# Revit family: FP_Revit_18_CG244DLPX1_N_Cooktop_90001824A
name_source: partatom
category: Specialty Equipment
revit_build: Autodesk Revit 2018 (Build: 20170223_1515(x64)
units: mm (PartAtom-declared; Revit-internal decimal feet)

## family parameters
Always vertical = Yes
Cut with Voids When Loaded = Yes
OmniClass Number = 23.40.40.00
OmniClass Title = Food Service Equipment and Furnishings
Part Type = Normal
Room Calculation Point = No
Round Connector Dimension = Use Diameter
Shared = No
Work Plane-Based = No

## types (2) — shared parameters
Cavity - Depth = 490 mm  [stored 1.60761 ft]
Cavity - Height = 59 mm
Cavity - Width = 560 mm  [stored 1.83727 ft]
Chassis - Depth = 486 mm
Chassis - Height = 59 mm
Chassis - Width = 555 mm  [stored 1.82087 ft]
Clearance - Below Combustible = 70 mm  [stored 0.229659 ft]
Clearance - Below Non-Combustible = 65 mm  [stored 0.213255 ft]
Clearance - Overhead Combustible = 762 mm  [stored 2.5 ft]
Clearance - Overhead Non-Combustible = 762 mm  [stored 2.5 ft]
Clearance - Overhead Rangehood = 762 mm  [stored 2.5 ft]
Clearance - Rear Combustible = 74 mm  [stored 0.242782 ft]
Clearance - Rear Non-Combustible = 38 mm  [stored 0.124672 ft]
Clearance - Side Combustible = 294 mm  [stored 0.964567 ft]
Clearance - Side Non-Combustible = 294 mm  [stored 0.964567 ft]
Connector Note - Electrical = 120 V, 60Hz
Description = 24" Gas on Stainless Cooktop
Manufacturer = Fisher & Paykel Appliances
Material - Body = Fisher & Paykel - Grey
Material - Burners & Trivets = Fisher & Paykel - Black, Matte
Material - Buttons and Dials = Fisher & Paykel - Stainless Steel
Material - Cooktop = Fisher & Paykel - Stainless Steel
Material - Trim = Fisher & Paykel - Steel, Chrome Plated
Product - Depth = 530 mm  [stored 1.73885 ft]
Product - Height = 108 mm  [stored 0.354331 ft]
Product - Width = 600 mm  [stored 1.9685 ft]
URL = www.fisherpaykel.com
Visibility - Clearance Required = Yes

## per-type parameters (varying)
| type | Connector Note - Gas |
| CG244DNGX1_N | NG 1 kPa (4" WC), Connection is Rp 1/2" (ISO7-1) |
| CG244DLPX1_N | LPG 2.75 kPa (11" WC), Connection is Rp 1/2" (ISO7-1) |

note: column(s) folded — value = type name in every type: Model

note: [stored X ft] marks values corroborated as IEEE doubles in the binary element streams (Revit-internal decimal feet)

## geometry (parser evidence)
native form markers: Sweep x23
no freeform markers — native parametric forms only
